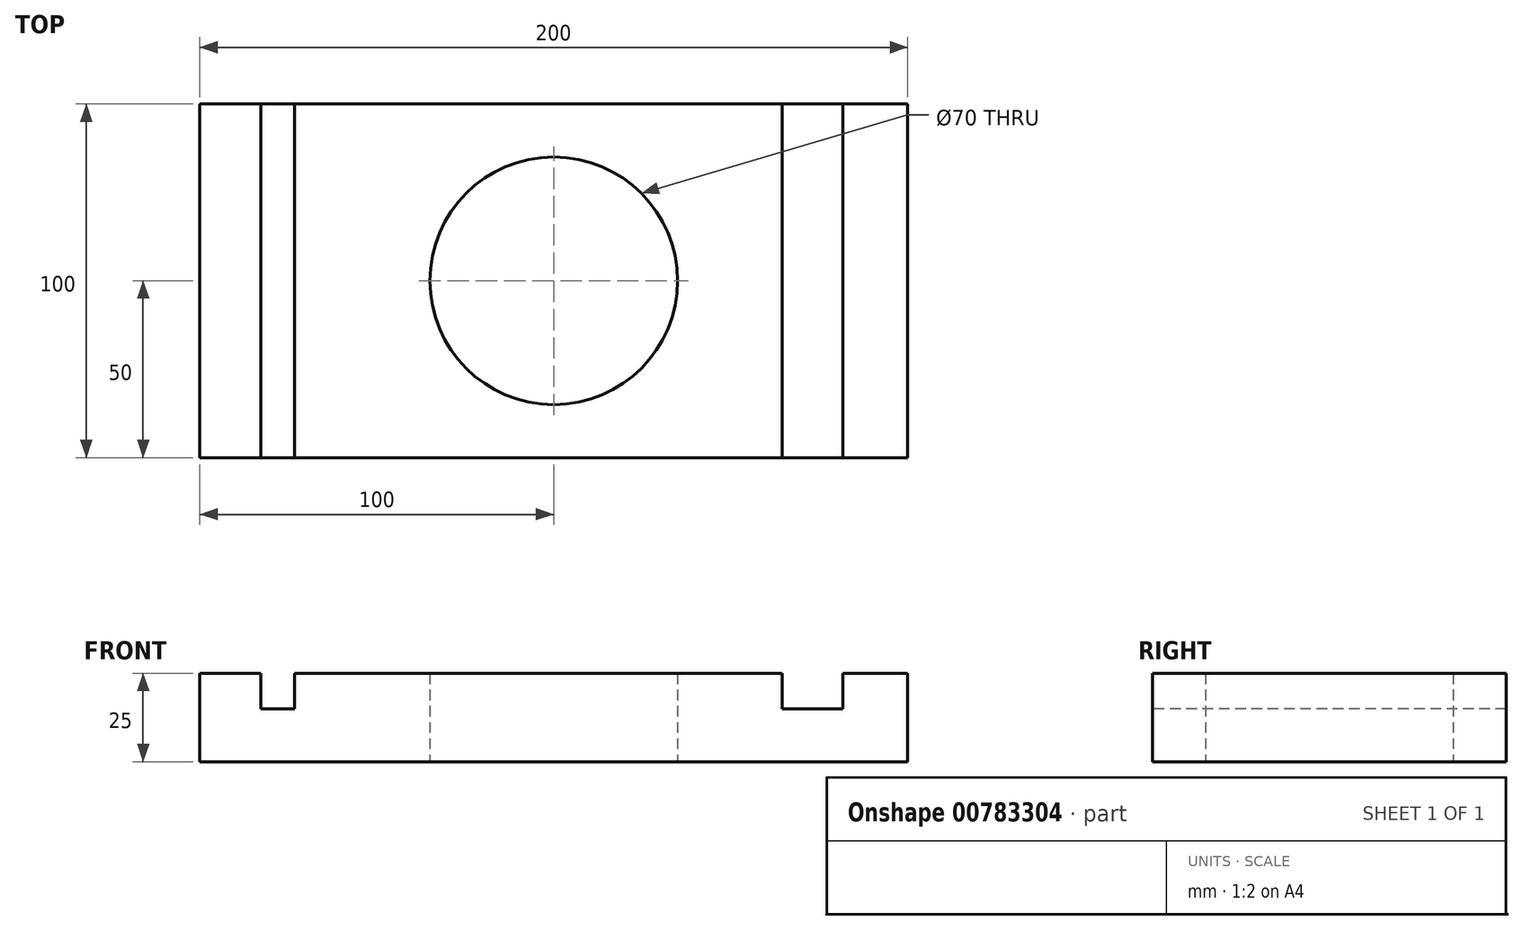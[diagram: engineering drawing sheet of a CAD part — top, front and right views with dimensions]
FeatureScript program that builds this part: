
annotation { "Feature Type Name" : "Feature", "Feature Type Description" : "" }
export const myFeature = defineFeature(function(context is Context, id is Id, definition is map)
    precondition{}
    {
        {
            var Q0;
            Q0=qCreatedBy(makeId("Top.planeOp"),FACE);
            var sketch = newSketch(context, id + "F0", { "sketchPlane" : qUnion([Q0])});
            skLineSegment(sketch, "E0.bottom", {"start": v(100, 50) * mm, "end": v(-100, 50) * mm});
            skLineSegment(sketch, "E0.top", {"start": v(100, -50) * mm, "end": v(-100, -50) * mm});
            skLineSegment(sketch, "E0.left", {"start": v(100, 50) * mm, "end": v(100, -50) * mm});
            skLineSegment(sketch, "E0.right", {"start": v(-100, 50) * mm, "end": v(-100, -50) * mm});
            skPoint(sketch, "E0.middle", {"position": v(0, 0) * mm});
            skCircle(sketch, "E1", {"center": v(0, 0) * mm, "radius": 35 * mm});
            skSolve(sketch);
        }
        {
            var Q0;
            Q0 = qSketchRegion(id + "F0", true);
            extrude(context, id + "F1", {"entities" : qUnion([Q0]), "depth" : 25 * mm, "offsetDistance" : 25 * mm});
        }
        {
            var Q0;
            Q0=makeQuery(id+"F1.opExtrude","CAP_FACE",FACE,{"disambiguationData":[OSD([sQuery(id+"F0.wireOp",EDGE,"E0.bottom"),sQuery(id+"F0.wireOp",EDGE,"E0.top"),sQuery(id+"F0.wireOp",EDGE,"E0.left"),sQuery(id+"F0.wireOp",EDGE,"E0.right"),sQuery(id+"F0.wireOp",EDGE,"E1")])],"isStart":false});
            var sketch = newSketch(context, id + "F2", { "sketchPlane" : qUnion([Q0])});
            skLineSegment(sketch, "E2.bottom", {"start": v(-82.77, 50) * mm, "end": v(-73.27, 50) * mm});
            skLineSegment(sketch, "E2.top", {"start": v(-82.77, -50) * mm, "end": v(-73.27, -50) * mm});
            skLineSegment(sketch, "E2.left", {"start": v(-82.77, 50) * mm, "end": v(-82.77, -50) * mm});
            skLineSegment(sketch, "E2.right", {"start": v(-73.27, 50) * mm, "end": v(-73.27, -50) * mm});
            skLineSegment(sketch, "E3.bottom", {"start": v(64.51, 50) * mm, "end": v(81.67, 50) * mm});
            skLineSegment(sketch, "E3.top", {"start": v(64.51, -50) * mm, "end": v(81.67, -50) * mm});
            skLineSegment(sketch, "E3.left", {"start": v(64.51, 50) * mm, "end": v(64.51, -50) * mm});
            skLineSegment(sketch, "E3.right", {"start": v(81.67, 50) * mm, "end": v(81.67, -50) * mm});
            skSolve(sketch);
        }
        {
            var Q0;
            Q0 = qSketchRegion(id + "F2", true);
            extrude(context, id + "F3", {"entities" : qUnion([Q0]), "operationType" : NewBodyOperationType.REMOVE, "oppositeDirection" : true, "depth" : 10 * mm, "offsetDistance" : 25 * mm});
        }
    });
